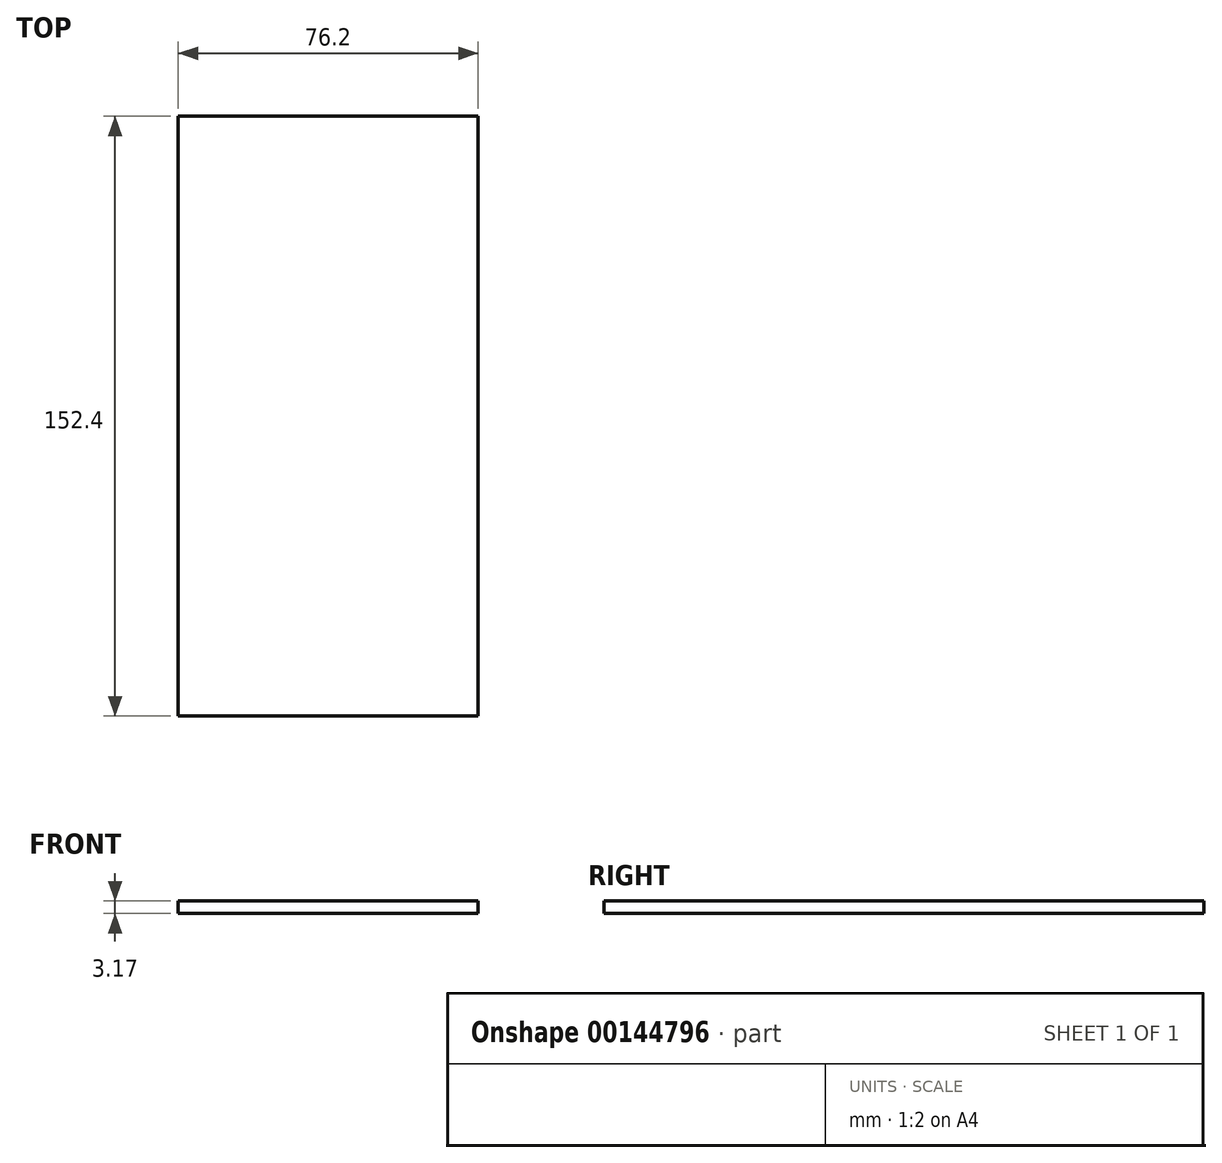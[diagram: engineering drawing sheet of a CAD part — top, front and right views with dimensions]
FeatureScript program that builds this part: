
annotation { "Feature Type Name" : "Feature", "Feature Type Description" : "" }
export const myFeature = defineFeature(function(context is Context, id is Id, definition is map)
    precondition{}
    {
        {
            var Q0;
            Q0=qCreatedBy(makeId("Top.planeOp"),FACE);
            var sketch = newSketch(context, id + "F0", { "sketchPlane" : qUnion([Q0])});
            skLineSegment(sketch, "E0.bottom", {"start": v(0, 0) * mm, "end": v(76.2, 0) * mm});
            skLineSegment(sketch, "E0.top", {"start": v(0, 152.4) * mm, "end": v(76.2, 152.4) * mm});
            skLineSegment(sketch, "E0.left", {"start": v(0, 0) * mm, "end": v(0, 152.4) * mm});
            skLineSegment(sketch, "E0.right", {"start": v(76.2, 0) * mm, "end": v(76.2, 152.4) * mm});
            skSolve(sketch);
        }
        {
            var Q0;
            Q0=makeQuery(id+"F0.imprint","IMPRINT",FACE,{"disambiguationData":[TD([[makeQuery(id+"F0.imprint","IMPRINT",EDGE,{"derivedFrom":sQuery(id+"F0.wireOp",EDGE,"E0.bottom")}),1.0]])]});
            extrude(context, id + "F1", {"entities" : qUnion([Q0]), "depth" : 3.17 * mm});
        }
    });
